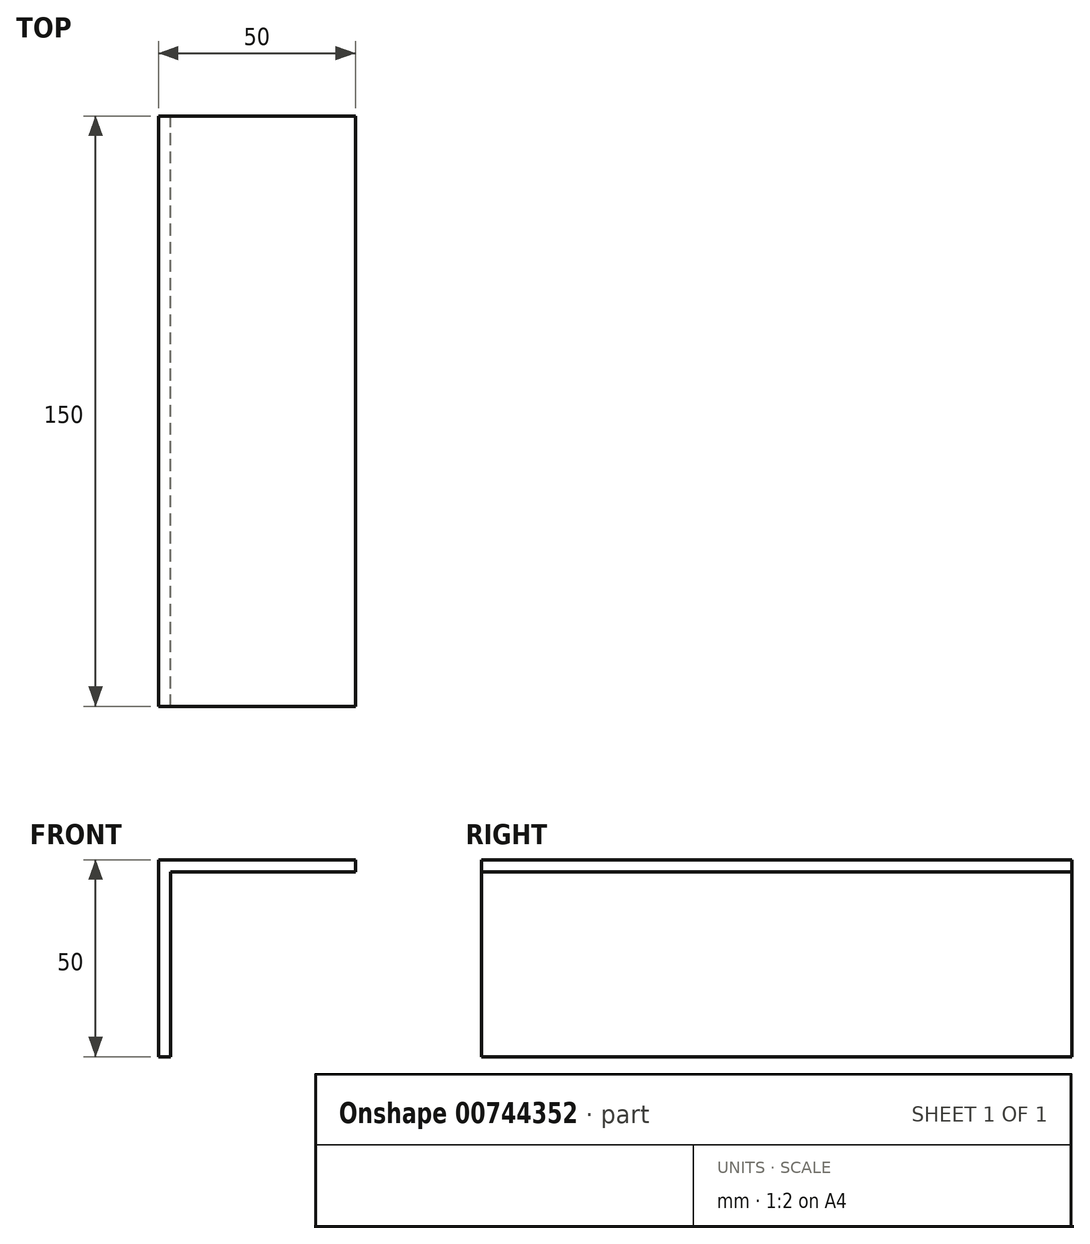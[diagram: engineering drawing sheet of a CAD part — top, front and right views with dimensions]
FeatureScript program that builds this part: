
annotation { "Feature Type Name" : "Feature", "Feature Type Description" : "" }
export const myFeature = defineFeature(function(context is Context, id is Id, definition is map)
    precondition{}
    {
        {
            var Q0;
            Q0=qCreatedBy(makeId("Front.planeOp"),FACE);
            var sketch = newSketch(context, id + "F0", { "sketchPlane" : qUnion([Q0])});
            skLineSegment(sketch, "E0.bottom", {"start": v(-22, -1.5) * mm, "end": v(25, -1.5) * mm});
            skLineSegment(sketch, "E0.top", {"start": v(-25, 1.5) * mm, "end": v(25, 1.5) * mm});
            skLineSegment(sketch, "E0.left", {"start": v(-25, -1.5) * mm, "end": v(-25, 1.5) * mm});
            skLineSegment(sketch, "E0.right", {"start": v(25, -1.5) * mm, "end": v(25, 1.5) * mm});
            skPoint(sketch, "E0.middle", {"position": v(0, 0) * mm});
            skLineSegment(sketch, "E1", {"start": v(-25, 1.5) * mm, "end": v(-25, -48.5) * mm});
            skLineSegment(sketch, "E2", {"start": v(-25, -48.5) * mm, "end": v(-22, -48.5) * mm});
            skLineSegment(sketch, "E3", {"start": v(-22, -48.5) * mm, "end": v(-22, -1.5) * mm});
            skPoint(sketch, "E4.orphan", {"position": v(-22, 1.5) * mm});
            skSolve(sketch);
        }
        {
            var Q0;
            Q0=makeQuery(id+"F0.imprint","IMPRINT",FACE,{"disambiguationData":[TD([[makeQuery(id+"F0.imprint","IMPRINT",EDGE,{"derivedFrom":sQuery(id+"F0.wireOp",EDGE,"E0.bottom")}),1.0]])]});
            extrude(context, id + "F1", {"entities" : qUnion([Q0]), "depth" : 150 * mm, "offsetDistance" : 25 * mm});
        }
    });
